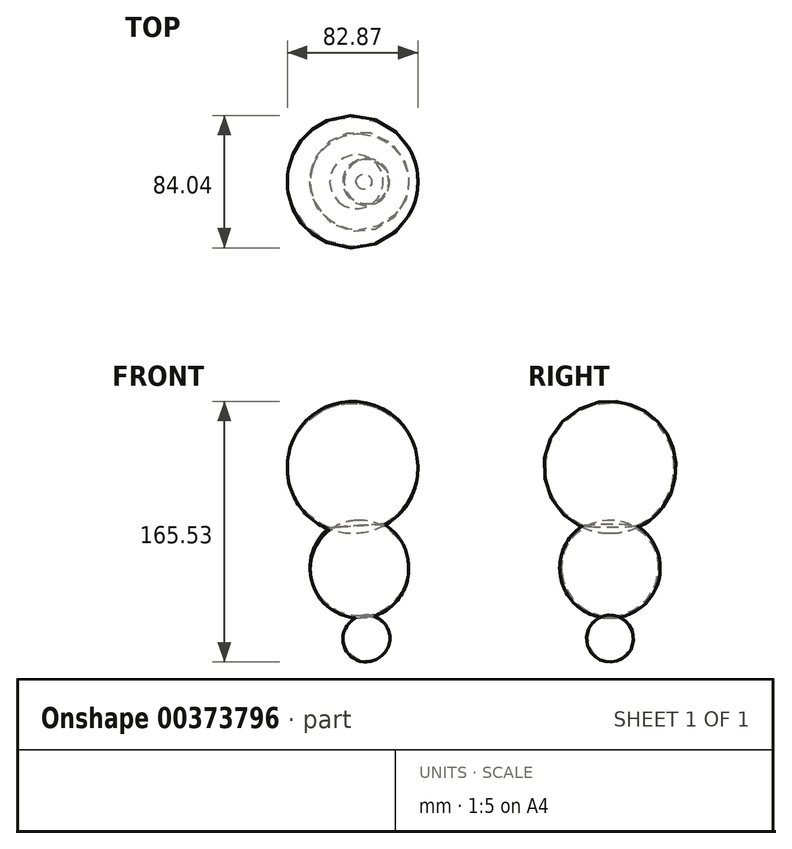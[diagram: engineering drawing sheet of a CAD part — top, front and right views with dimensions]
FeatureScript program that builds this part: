
annotation { "Feature Type Name" : "Feature", "Feature Type Description" : "" }
export const myFeature = defineFeature(function(context is Context, id is Id, definition is map)
    precondition{}
    {
        {
            var Q0;
            Q0=qCreatedBy(makeId("Front.planeOp"),FACE);
            var sketch = newSketch(context, id + "F0", { "sketchPlane" : qUnion([Q0])});
            skArc(sketch, "E0", {"start": v(0, -63.55) * mm, "mid": v(0.37, -43.2) * mm, "end": v(-19.97, -42.23) * mm});
            skLineSegment(sketch, "E1", {"start": v(-19.97, -42.23) * mm, "end": v(0, -63.55) * mm});
            skSolve(sketch);
        }
        {
            var Q0;
            Q0 = qSketchRegion(id + "F0", true);
            var Q1;
            Q1=sQuery(id+"F0.wireOp",EDGE,"E1");
            revolve(context, id + "F1", {"entities" : qUnion([Q0]), "axis" : qUnion([Q1]), "revolveType" : RevolveType.FULL});
        }
        {
            var Q0;
            Q0=qCreatedBy(makeId("Front.planeOp"),FACE);
            var sketch = newSketch(context, id + "F2", { "sketchPlane" : qUnion([Q0])});
            skArc(sketch, "E2", {"start": v(-45.6, -10.39) * mm, "mid": v(-12.1, -39.93) * mm, "end": v(16.73, -5.8) * mm});
            skLineSegment(sketch, "E3", {"start": v(-45.6, -10.39) * mm, "end": v(16.73, -5.8) * mm});
            skSolve(sketch);
        }
        {
            var Q0;
            Q0 = qSketchRegion(id + "F2", true);
            var Q1;
            Q1=sQuery(id+"F2.wireOp",EDGE,"E3");
            revolve(context, id + "F3", {"operationType" : NewBodyOperationType.ADD, "entities" : qUnion([Q0]), "axis" : qUnion([Q1]), "revolveType" : RevolveType.FULL});
        }
        {
            var Q0;
            Q0=qCreatedBy(makeId("Front.planeOp"),FACE);
            var sketch = newSketch(context, id + "F4", { "sketchPlane" : qUnion([Q0])});
            skArc(sketch, "E4", {"start": v(-60.18, 55.18) * mm, "mid": v(-18.22, 14.89) * mm, "end": v(22.67, 56.26) * mm});
            skLineSegment(sketch, "E5", {"start": v(-60.18, 55.18) * mm, "end": v(22.67, 56.26) * mm});
            skSolve(sketch);
        }
        {
            var Q0;
            Q0 = qSketchRegion(id + "F4", true);
            var Q1;
            Q1=sQuery(id+"F4.wireOp",EDGE,"E5");
            revolve(context, id + "F5", {"operationType" : NewBodyOperationType.ADD, "entities" : qUnion([Q0]), "axis" : qUnion([Q1]), "revolveType" : RevolveType.FULL});
        }
    });
